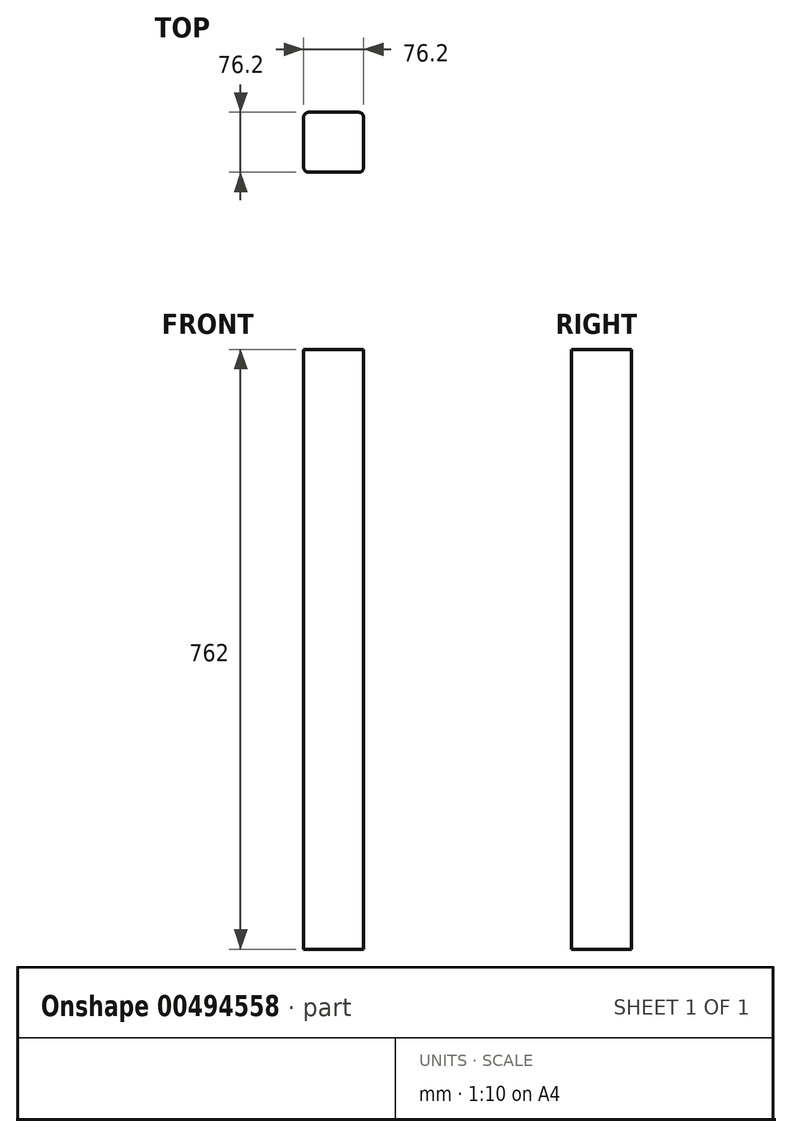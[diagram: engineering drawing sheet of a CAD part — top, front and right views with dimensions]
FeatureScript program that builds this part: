
annotation { "Feature Type Name" : "Feature", "Feature Type Description" : "" }
export const myFeature = defineFeature(function(context is Context, id is Id, definition is map)
    precondition{}
    {
        {
            var Q0;
            Q0=qCreatedBy(makeId("Top.planeOp"),FACE);
            var sketch = newSketch(context, id + "F0", { "sketchPlane" : qUnion([Q0])});
            skLineSegment(sketch, "E0.bottom", {"start": v(-6.35, 0) * mm, "end": v(-69.85, 0) * mm});
            skLineSegment(sketch, "E0.top", {"start": v(-6.35, -76.2) * mm, "end": v(-69.85, -76.2) * mm});
            skLineSegment(sketch, "E0.left", {"start": v(0, -6.35) * mm, "end": v(0, -69.85) * mm});
            skLineSegment(sketch, "E0.right", {"start": v(-76.2, -6.35) * mm, "end": v(-76.2, -69.85) * mm});
            skPoint(sketch, "E1.visualSharp", {"position": v(-76.2, -76.2) * mm});
            skArc(sketch, "E1.filletArc", {"start": v(-76.2, -69.85) * mm, "mid": v(-74.34, -74.34) * mm, "end": v(-69.85, -76.2) * mm});
            skPoint(sketch, "E2.visualSharp", {"position": v(0, -76.2) * mm});
            skArc(sketch, "E2.filletArc", {"start": v(-6.35, -76.2) * mm, "mid": v(-1.86, -74.34) * mm, "end": v(0, -69.85) * mm});
            skPoint(sketch, "E3.visualSharp", {"position": v(0, 0) * mm});
            skArc(sketch, "E3.filletArc", {"start": v(0, -6.35) * mm, "mid": v(-1.86, -1.86) * mm, "end": v(-6.35, 0) * mm});
            skPoint(sketch, "E4.visualSharp", {"position": v(-76.2, 0) * mm});
            skArc(sketch, "E4.filletArc", {"start": v(-69.85, 0) * mm, "mid": v(-74.34, -1.86) * mm, "end": v(-76.2, -6.35) * mm});
            skSolve(sketch);
        }
        {
            var Q0;
            Q0=makeQuery(id+"F0.imprint","IMPRINT",FACE,{"disambiguationData":[TD([[makeQuery(id+"F0.imprint","IMPRINT",EDGE,{"derivedFrom":sQuery(id+"F0.wireOp",EDGE,"E0.bottom")}),1.0]])]});
            extrude(context, id + "F1", {"entities" : qUnion([Q0]), "depth" : 762 * mm});
        }
    });
